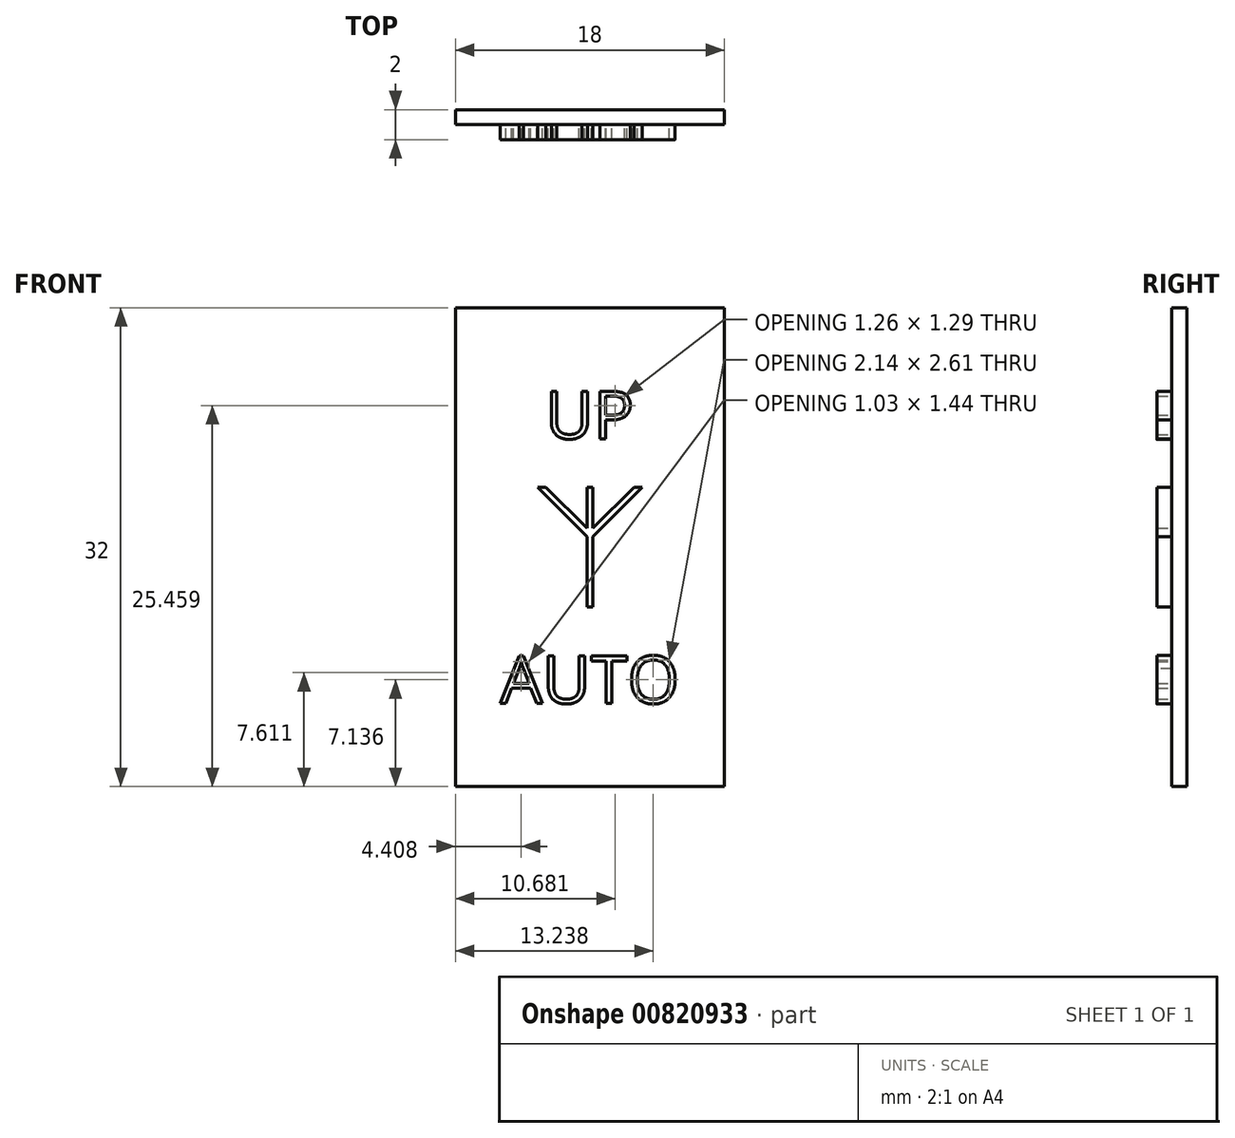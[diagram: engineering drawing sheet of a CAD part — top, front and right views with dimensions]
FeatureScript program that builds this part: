
annotation { "Feature Type Name" : "Feature", "Feature Type Description" : "" }
export const myFeature = defineFeature(function(context is Context, id is Id, definition is map)
    precondition{}
    {
        {
            var Q0;
            Q0=qCreatedBy(makeId("Front.planeOp"),FACE);
            var sketch = newSketch(context, id + "F0", { "sketchPlane" : qUnion([Q0])});
            skLineSegment(sketch, "E0", {"start": v(0, 4) * mm, "end": v(0, -4) * mm});
            skLineSegment(sketch, "E1", {"start": v(0, 0.78) * mm, "end": v(3.22, 4) * mm});
            skLineSegment(sketch, "E2.MirrorCS", {"start": v(0, 0.78) * mm, "end": v(-3.22, 4) * mm});
            skText(sketch, "E3", { "text": "UP", "fontName": "OpenSans-Regular.ttf"});
            skText(sketch, "E4", { "text": "AUTO", "fontName": "OpenSans-Regular.ttf"});
            const initialGuessF0  = {"E3": [-0.00299, 0.00725, 1, 0, 0.0032], "E4": [-0.006, -0.01045, 1, 0, 0.0032]};
            skSetInitialGuess(sketch, initialGuessF0);
            skSolve(sketch);
        }
        {
            var Q0;
            Q0=qSketchRegion(id+"F0",true);
            extrude(context, id + "F1", {"entities" : qUnion([Q0]), "depth" : 1 * mm, "offsetDistance" : 25 * mm});
        }
        {
            var Q0;
            Q0=qCreatedBy(makeId("Front.planeOp"),FACE);
            var sketch = newSketch(context, id + "F2", { "sketchPlane" : qUnion([Q0])});
            skLineSegment(sketch, "E5.bottom", {"start": v(-0.2, 4) * mm, "end": v(0.2, 4) * mm});
            skLineSegment(sketch, "E5.top", {"start": v(-0.2, -4) * mm, "end": v(0.2, -4) * mm});
            skLineSegment(sketch, "E5.left", {"start": v(-0.2, 4) * mm, "end": v(-0.2, -4) * mm});
            skLineSegment(sketch, "E5.right", {"start": v(0.2, 4) * mm, "end": v(0.2, -4) * mm});
            skLineSegment(sketch, "E6", {"start": v(3.5, 4) * mm, "end": v(0, 0.5) * mm});
            skLineSegment(sketch, "E7", {"start": v(0, 0.5) * mm, "end": v(-3.5, 4) * mm});
            skLineSegment(sketch, "E8", {"start": v(-3.5, 4) * mm, "end": v(-2.94, 4) * mm});
            skLineSegment(sketch, "E9", {"start": v(-2.94, 4) * mm, "end": v(0, 1.06) * mm});
            skLineSegment(sketch, "E10", {"start": v(0, 1.06) * mm, "end": v(2.94, 4) * mm});
            skLineSegment(sketch, "E11", {"start": v(2.94, 4) * mm, "end": v(3.5, 4) * mm});
            skSolve(sketch);
        }
        {
            var Q0;
            Q0=qSketchRegion(id+"F2",true);
            extrude(context, id + "F3", {"entities" : qUnion([Q0]), "depth" : 1 * mm, "offsetDistance" : 25 * mm});
        }
        {
            var Q0;
            Q0=qCreatedBy(makeId("Front.planeOp"),FACE);
            var sketch = newSketch(context, id + "F4", { "sketchPlane" : qUnion([Q0])});
            skLineSegment(sketch, "E12.bottom", {"start": v(-9, 16) * mm, "end": v(9, 16) * mm});
            skLineSegment(sketch, "E12.top", {"start": v(-9, -16) * mm, "end": v(9, -16) * mm});
            skLineSegment(sketch, "E12.left", {"start": v(-9, 16) * mm, "end": v(-9, -16) * mm});
            skLineSegment(sketch, "E12.right", {"start": v(9, 16) * mm, "end": v(9, -16) * mm});
            skSolve(sketch);
        }
        {
            var Q0;
            Q0=qSketchRegion(id+"F4",true);
            extrude(context, id + "F5", {"entities" : qUnion([Q0]), "depth" : -1 * mm, "offsetDistance" : 25 * mm});
        }
    });
